# Revit family: 2CKA006800A2740
name_source: partatom
category: Elektroinstallationen
revit_build: Autodesk Revit 2017 (Build: 20160225_1515(x64)
units: mm (PartAtom-declared; Revit-internal decimal feet)

## family parameters
Basisbauteil = Fläche
Beim Laden mit Abzugskörper schneiden = Nein
Bemaßung runder Anschluss = Durchmesser verwenden
Beschriftungsausrichtung beibehalten = Nein
Gemeinsam genutzt = Nein
Raumberechnungspunkt = Nein
Teiletyp = Normal

## types (1)
- 2CKA006800A2740
    Ansprechempfindlichkeit einstellbar = Ja
    Ansprechhelligkeit [lx] = [5:2000]
    Ansprechhelligkeit einstellbar = Ja
    Anzahl der Schaltzonen = 640
    Ausführung = Präsenzmelder
    Ausführung der Oberfläche = matt
    BIM = https://media.live.bim.site
    BIMSITE_PRODUCT_ID = 3cb81b51527aa5d17008f66e9f741f984a8873fe
    Beschreibung = Busch-Präsenzmelder Universal BT, Relais, studioweiß matt, Bewegungs-/Präsenzmelder, Präsenzmelder, Busch-Präsenzmelder Universal BT, Relais 12 Meter Master-Präsenzmelder mit Mischlichtmessung. Zum helligkeits- und bewegungsabhängigen Schalten von Beleuchtungen. Mit Bluetooth-Schnittstelle zur Parametrierung und Bedienung. Anpassung sämtlicher Einstellmöglichkeiten über Smartphone oder Tablet. Lichtsteuerung über Smartphone oder Tablet App. Mit Hochlastrelais für LED-Betrieb. Erfassungsbereich (bei 3 m Montagehöhe): kreisförmig: Sitzende Personen: bis zu Ø 10 m, gehende Personen: bis zu Ø 12 m. Erweiterung des Erfassungsbereiches durch Master-/Slave Kombination. Aufbauhöhe 23 mm. Für halbautomatischen, Komfort- und vollautomatischen Betrieb. Zusätzliche Ein-/Ausschaltmöglichkeit über Tastereingang. Mit Dauerlicht- / Dauer-Aus-Funktion (8 Std.), über intelligenten Nebenstelleneingang aktivierbar. Mit wählbarer Anwesenheitssimulation bei Nichtanwesenheit. Mit integrierter Speicherung der Einschaltdauer (Energie Monitor). Mit helligkeitsunabhängigem Testbetrieb zur Auswertung des Erfassungsbereiches. Mit Teach-In Funktion der Helligkeitsschaltschwelle, IR Service-Handsender erforderlich. Mit Erfassungsanzeige im Testbetrieb. Deckeneinbaumontage über integrierte Federbügel. Verdrehschutz über zusätzliche Schnellverspannung. Einstellelemente frontseitig zugänglich. Überwachungsdichte: 72 Sektoren mit 640 Schaltsegmenten. Individuelle Abschaltung und Empfindlichkeitseinstellung einzelner Sensoren möglich. Ausschaltverzögerung: ca. 1 Min. - 30 Min. oder Kurzzeitimpuls einstellbar. Mit wählbarer dynamischer Ausschaltverzögerung. Geeignet für abgehängte Decken mit eine Plattenstärke von 9 bis 25 mm. Einbaulochmaß: Ø 68 mm. Bedienelemente: 2 Regler zur Einstellung von Helligkeitsschaltschwelle und Nachlaufzeit. Anzeigeelemente: LED Erfassungs- und Statusanzeige. Nennspannung: 230 V~, +10 % / -10 % Nennfrequenz: 50 Hz/60 Hz Ausgänge: 1x Schließer, potenzialgebunden Lastart: 230 V-Glühlampen Nennleistung: 2300 W Lastart: 230 V~ LEDi Nennleistung: 200 W/VA Lastart: Leuchtstofflampen Nennstrom: 10 AX, bei cos ? 0,9 Öffnungswinkel: 360 ° Helligkeitsgrenzwert: 5 Lux - 2000 Lux Montagehöhe: 2 m - 4 m Schutzart Gerät: IP 40 Temperaturbereich Gerät: -5 °C bis 45 °C Maße (H x B x T): 94 mm x 94 mm x 72 mm Einbautiefe: 49 mm 60669-2-1
    Datenblatt = https://media.live.bim.site
    Erfassungsfeld Durchmesser auf Fußboden [m] = 12
    Erfassungswinkel horizontal [°] = [90:360]
    Farbe = weiß
    Fernbedienbar = Ja
    Frequenz [Hz] = [50:60]
    GTIN = 4011395217627
    Geeignet für C-Last = Ja
    Gerätebreite [mm] = 94
    Gerätehöhe [mm] = 94
    Gerätetiefe [mm] = 72
    Gewicht [kg/m] = 0.161
    HAN = 2CKA006800A2740
    Halogenfrei = Ja
    HeinzeBIM = https://www.heinze.de
    Hersteller = Busch-Jaeger
    Ist System = Nein
    Ist Zubehör = Nein
    Max. Einschaltdauer [s] = 1800
    Max. Einschaltstrom = 800 A
    Max. Reichweite frontal [m] = 6
    Max. Reichweite zu einer Seite [m] = 6
    Max. Schaltleistung [Voltampere] = 2300
    Min. Einschaltdauer [s] = 60
    Montageart = sonstige
    Nebenstelleneingang = Ja
    Nennspannung [V] [Volt] = 230
    Oberfläche = unbehandelt
    Optimale Montagehöhe [m] = 3
    Produktseite = https://media.live.bim.site
    RAL-Nummer (ähnlich) = 9016
    Schutzart (IP) = IP40
    Sensortyp = passiv Infrarot
    Spannungsart = AC
    TYPE = 6819/31-24
    Teach-Funktion für Ansprechhelligkeit = Ja
    Temperatur [K] = [-5:45]
    Treppenhausüberwachung = Ja
    Typname = Busch-Präsenzmelder Universal BT, Relais, studioweiß matt, Bewegungs-/Präsenzmelder, Präsenzmelder
    URL = https://www.busch-jaeger.de
    Unterkriechschutz/Rückfeldüberwachung = Ja
    Vorgabe-Ansicht = 1219 mm
    Werkstoff = Kunststoff
    Werkstoffgüte = Thermoplast

## geometry (parser evidence)
native form markers: Sweep x3
no freeform markers — native parametric forms only
